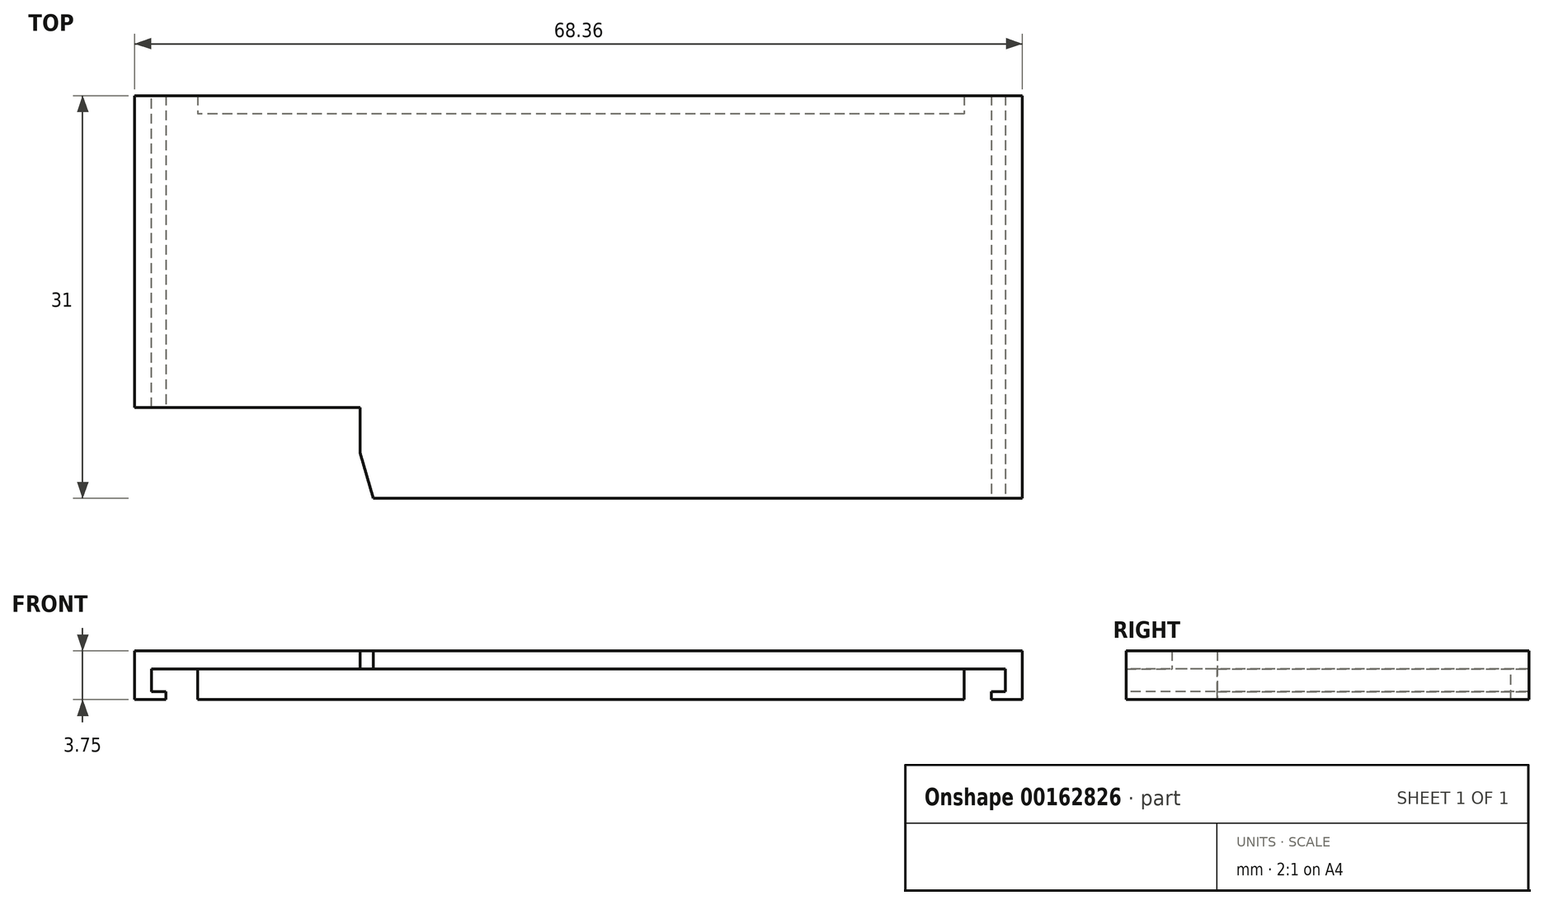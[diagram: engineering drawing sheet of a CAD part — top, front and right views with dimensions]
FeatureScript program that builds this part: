
annotation { "Feature Type Name" : "Feature", "Feature Type Description" : "" }
export const myFeature = defineFeature(function(context is Context, id is Id, definition is map)
    precondition{}
    {
        {
            var Q0;
            Q0=qCreatedBy(makeId("Top.planeOp"),FACE);
            var sketch = newSketch(context, id + "F0", { "sketchPlane" : qUnion([Q0])});
            skLineSegment(sketch, "E0", {"start": v(0, 0) * mm, "end": v(68.36, 0) * mm});
            skLineSegment(sketch, "E1", {"start": v(68.36, 0) * mm, "end": v(68.36, -31) * mm});
            skLineSegment(sketch, "E2", {"start": v(68.36, -31) * mm, "end": v(18.36, -31) * mm});
            skLineSegment(sketch, "E3", {"start": v(18.36, -31) * mm, "end": v(17.36, -27.5) * mm});
            skLineSegment(sketch, "E4", {"start": v(17.36, -24) * mm, "end": v(0, -24) * mm});
            skLineSegment(sketch, "E5", {"start": v(0, -24) * mm, "end": v(0, 0) * mm});
            skLineSegment(sketch, "E6", {"start": v(17.36, -24) * mm, "end": v(17.36, -27.5) * mm});
            skSolve(sketch);
        }
        {
            var Q0;
            Q0 = qSketchRegion(id + "F0", true);
            extrude(context, id + "F1", {"entities" : qUnion([Q0]), "depth" : 1.4 * mm});
        }
        {
            var Q0;
            Q0=makeQuery(id+"F1.opExtrude","CAP_FACE",FACE,{"disambiguationData":[OSD([sQuery(id+"F0.wireOp",EDGE,"E0"),sQuery(id+"F0.wireOp",EDGE,"E1"),sQuery(id+"F0.wireOp",EDGE,"E2"),sQuery(id+"F0.wireOp",EDGE,"E3"),sQuery(id+"F0.wireOp",EDGE,"E4"),sQuery(id+"F0.wireOp",EDGE,"E5"),sQuery(id+"F0.wireOp",EDGE,"E6")])],"isStart":true});
            var sketch = newSketch(context, id + "F2", { "sketchPlane" : qUnion([Q0])});
            skLineSegment(sketch, "E7.bottom", {"start": v(68.36, 0) * mm, "end": v(67.06, 0) * mm});
            skLineSegment(sketch, "E7.top", {"start": v(68.36, 31) * mm, "end": v(67.06, 31) * mm});
            skLineSegment(sketch, "E7.left", {"start": v(68.36, 0) * mm, "end": v(68.36, 31) * mm});
            skLineSegment(sketch, "E7.right", {"start": v(67.06, 0) * mm, "end": v(67.06, 31) * mm});
            skLineSegment(sketch, "E8.bottom", {"start": v(0, 24) * mm, "end": v(1.3, 24) * mm});
            skLineSegment(sketch, "E8.top", {"start": v(0, 0) * mm, "end": v(1.3, 0) * mm});
            skLineSegment(sketch, "E8.left", {"start": v(0, 24) * mm, "end": v(0, 0) * mm});
            skLineSegment(sketch, "E8.right", {"start": v(1.3, 24) * mm, "end": v(1.3, 0) * mm});
            skLineSegment(sketch, "E9.bottom", {"start": v(63.86, 0) * mm, "end": v(4.86, 0) * mm});
            skLineSegment(sketch, "E9.top", {"start": v(63.86, 1.4) * mm, "end": v(4.86, 1.4) * mm});
            skLineSegment(sketch, "E9.left", {"start": v(63.86, 0) * mm, "end": v(63.86, 1.4) * mm});
            skLineSegment(sketch, "E9.right", {"start": v(4.86, 0) * mm, "end": v(4.86, 1.4) * mm});
            skSolve(sketch);
        }
        {
            var Q0;
            Q0 = qSketchRegion(id + "F2", true);
            extrude(context, id + "F3", {"entities" : qUnion([Q0]), "operationType" : NewBodyOperationType.ADD, "depth" : 1.75 * mm});
        }
        {
            var Q0;
            Q0=makeQuery(id+"F3.opExtrude","CAP_FACE",FACE,{"disambiguationData":[OSD([sQuery(id+"F2.wireOp",EDGE,"E7.bottom"),sQuery(id+"F2.wireOp",EDGE,"E7.top"),sQuery(id+"F2.wireOp",EDGE,"E7.left"),sQuery(id+"F2.wireOp",EDGE,"E7.right")])],"isStart":false});
            var sketch = newSketch(context, id + "F4", { "sketchPlane" : qUnion([Q0])});
            skLineSegment(sketch, "E10.bottom", {"start": v(68.36, 0) * mm, "end": v(65.96, 0) * mm});
            skLineSegment(sketch, "E10.top", {"start": v(68.36, 31) * mm, "end": v(65.96, 31) * mm});
            skLineSegment(sketch, "E10.left", {"start": v(68.36, 0) * mm, "end": v(68.36, 31) * mm});
            skLineSegment(sketch, "E10.right", {"start": v(65.96, 0) * mm, "end": v(65.96, 31) * mm});
            skLineSegment(sketch, "E11.bottom", {"start": v(0, 0) * mm, "end": v(2.4, 0) * mm});
            skLineSegment(sketch, "E11.top", {"start": v(0, 24) * mm, "end": v(2.4, 24) * mm});
            skLineSegment(sketch, "E11.left", {"start": v(0, 0) * mm, "end": v(0, 24) * mm});
            skLineSegment(sketch, "E11.right", {"start": v(2.4, 0) * mm, "end": v(2.4, 24) * mm});
            skLineSegment(sketch, "E12.bottom", {"start": v(63.86, 1.4) * mm, "end": v(4.86, 1.4) * mm});
            skLineSegment(sketch, "E12.top", {"start": v(63.86, 0) * mm, "end": v(4.86, 0) * mm});
            skLineSegment(sketch, "E12.left", {"start": v(63.86, 1.4) * mm, "end": v(63.86, 0) * mm});
            skLineSegment(sketch, "E12.right", {"start": v(4.86, 1.4) * mm, "end": v(4.86, 0) * mm});
            skSolve(sketch);
        }
        {
            var Q0;
            Q0 = qSketchRegion(id + "F4", true);
            extrude(context, id + "F5", {"entities" : qUnion([Q0]), "operationType" : NewBodyOperationType.ADD, "depth" : 0.6 * mm});
        }
    });
